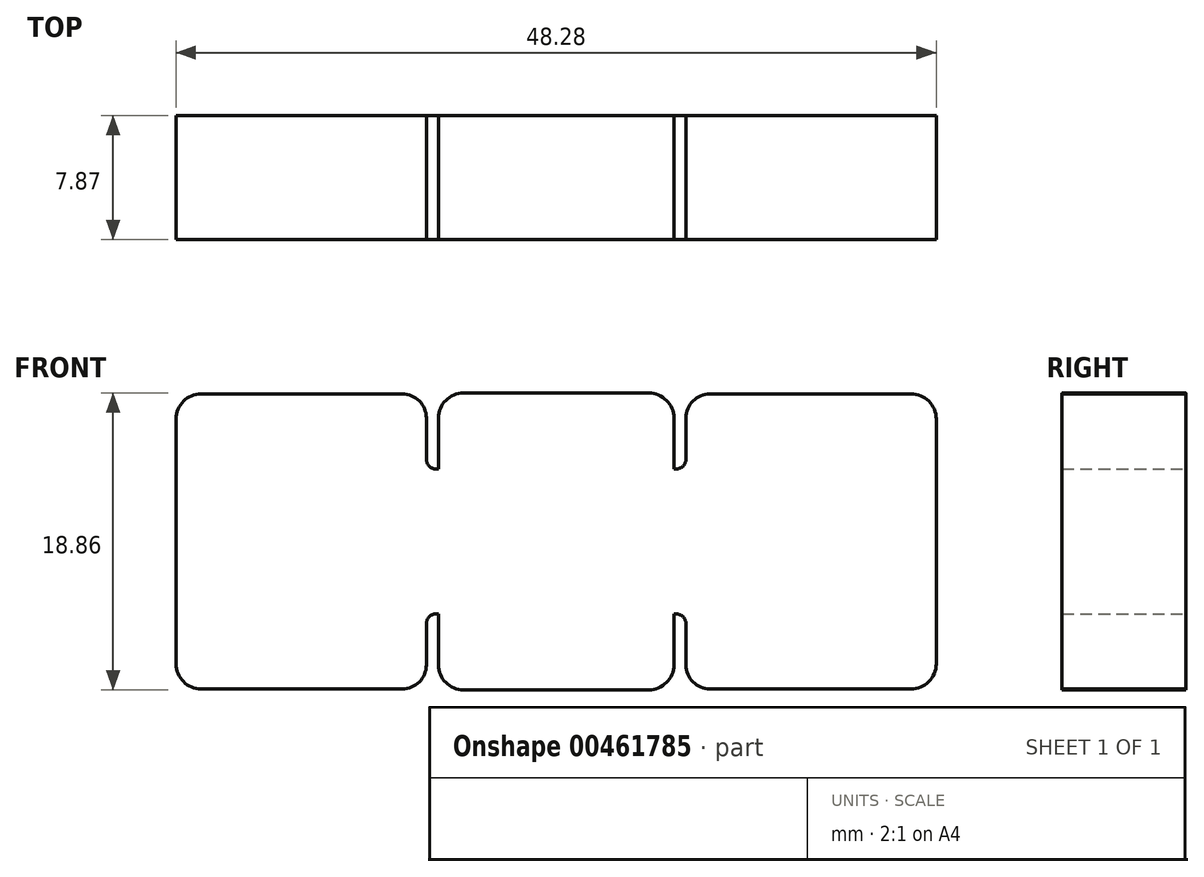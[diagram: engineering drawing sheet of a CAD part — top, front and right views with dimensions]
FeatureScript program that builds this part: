
annotation { "Feature Type Name" : "Feature", "Feature Type Description" : "" }
export const myFeature = defineFeature(function(context is Context, id is Id, definition is map)
    precondition{}
    {
        {
            var Q0;
            Q0=qCreatedBy(makeId("Front.planeOp"),FACE);
            var sketch = newSketch(context, id + "F0", { "sketchPlane" : qUnion([Q0])});
            skLineSegment(sketch, "E0", {"start": v(-7.48, 4.6) * mm, "end": v(-8.24, 4.6) * mm});
            skLineSegment(sketch, "E1", {"start": v(-8.24, 4.6) * mm, "end": v(-8.24, 9.37) * mm});
            skLineSegment(sketch, "E2", {"start": v(-8.24, 9.37) * mm, "end": v(-24.14, 9.37) * mm});
            skLineSegment(sketch, "E3", {"start": v(-24.14, 9.37) * mm, "end": v(-24.14, 0) * mm});
            skLineSegment(sketch, "E4", {"start": v(-7.48, 4.6) * mm, "end": v(-7.48, 9.43) * mm});
            skLineSegment(sketch, "E5", {"start": v(-7.48, 9.43) * mm, "end": v(0, 9.43) * mm});
            skLineSegment(sketch, "E6", {"start": v(-24.14, 0) * mm, "end": v(0, 0) * mm});
            skLineSegment(sketch, "E7", {"start": v(0, 0) * mm, "end": v(0, 9.43) * mm});
            skSolve(sketch);
        }
        {
            var Q0;
            Q0=makeQuery(id+"F0.imprint","IMPRINT",FACE,{"disambiguationData":[TD([[makeQuery(id+"F0.imprint","IMPRINT",EDGE,{"derivedFrom":sQuery(id+"F0.wireOp",EDGE,"E0")}),1.0]])]});
            extrude(context, id + "F1", {"entities" : qUnion([Q0]), "depth" : 7.87 * mm});
        }
        {
            var Q0;
            Q0=makeQuery(id+"F1.opExtrude","SWEPT_EDGE",EDGE,{"disambiguationData":[OSD([sQuery(id+"F0.wireOp",EDGE,"E1"),sQuery(id+"F0.wireOp",EDGE,"E2")])]});
            fillet(context, id + "F2", {"entities" : qUnion([Q0]), "radius" : 1.53 * mm, "tangentPropagation" : true, "allowEdgeOverflow" : false});
        }
        {
            var Q0;
            Q0=makeQuery(id+"F1.opExtrude","SWEPT_EDGE",EDGE,{"disambiguationData":[OSD([sQuery(id+"F0.wireOp",EDGE,"E2"),sQuery(id+"F0.wireOp",EDGE,"E3")])]});
            var Q1;
            Q1=makeQuery(id+"F1.opExtrude","SWEPT_EDGE",EDGE,{"disambiguationData":[OSD([sQuery(id+"F0.wireOp",EDGE,"E4"),sQuery(id+"F0.wireOp",EDGE,"E5")])]});
            fillet(context, id + "F3", {"entities" : qUnion([Q0, Q1]), "radius" : 1.6 * mm, "tangentPropagation" : true, "allowEdgeOverflow" : false});
        }
        {
            var Q0;
            Q0=makeQuery(id+"F1.opExtrude","SWEPT_EDGE",EDGE,{"disambiguationData":[OSD([sQuery(id+"F0.wireOp",EDGE,"E0"),sQuery(id+"F0.wireOp",EDGE,"E1")])]});
            fillet(context, id + "F4", {"entities" : qUnion([Q0]), "radius" : 0.61 * mm, "tangentPropagation" : true, "allowEdgeOverflow" : false});
        }
        {
            var Q0;
            Q0=makeQuery(id+"F1.opExtrude","SWEPT_BODY",BODY,{"disambiguationData":[OSD([sQuery(id+"F0.wireOp",EDGE,"E0"),sQuery(id+"F0.wireOp",EDGE,"E1"),sQuery(id+"F0.wireOp",EDGE,"E2"),sQuery(id+"F0.wireOp",EDGE,"E3"),sQuery(id+"F0.wireOp",EDGE,"E4"),sQuery(id+"F0.wireOp",EDGE,"E5"),sQuery(id+"F0.wireOp",EDGE,"E6"),sQuery(id+"F0.wireOp",EDGE,"E7")])]});
            var Q1;
            Q1=makeQuery(id+"F1.opExtrude","SWEPT_FACE",FACE,{"disambiguationData":[OSD([sQuery(id+"F0.wireOp",EDGE,"E7")])]});
            mirror(context, id + "F5", {"operationType" : NewBodyOperationType.ADD, "entities" : qUnion([Q0]), "mirrorPlane" : qUnion([Q1])});
        }
        {
            var Q0;
            Q0=makeQuery(id+"F1.opExtrude","SWEPT_BODY",BODY,{"disambiguationData":[OSD([sQuery(id+"F0.wireOp",EDGE,"E0"),sQuery(id+"F0.wireOp",EDGE,"E1"),sQuery(id+"F0.wireOp",EDGE,"E2"),sQuery(id+"F0.wireOp",EDGE,"E3"),sQuery(id+"F0.wireOp",EDGE,"E4"),sQuery(id+"F0.wireOp",EDGE,"E5"),sQuery(id+"F0.wireOp",EDGE,"E6"),sQuery(id+"F0.wireOp",EDGE,"E7")])]});
            var Q1;
            {var subQ0=makeQuery(id+"F1.opExtrude","SWEPT_FACE",FACE,{"disambiguationData":[OSD([sQuery(id+"F0.wireOp",EDGE,"E6")])]});Q1=makeQuery(id+"F5.boolean.opBoolean","MERGE",FACE,{"derivedFrom":[subQ0,makeQuery(id+"F5.opPattern","COPY",FACE,{"derivedFrom":subQ0,"instanceName":"1"})]});}
            mirror(context, id + "F6", {"operationType" : NewBodyOperationType.ADD, "entities" : qUnion([Q0]), "mirrorPlane" : qUnion([Q1])});
        }
    });
